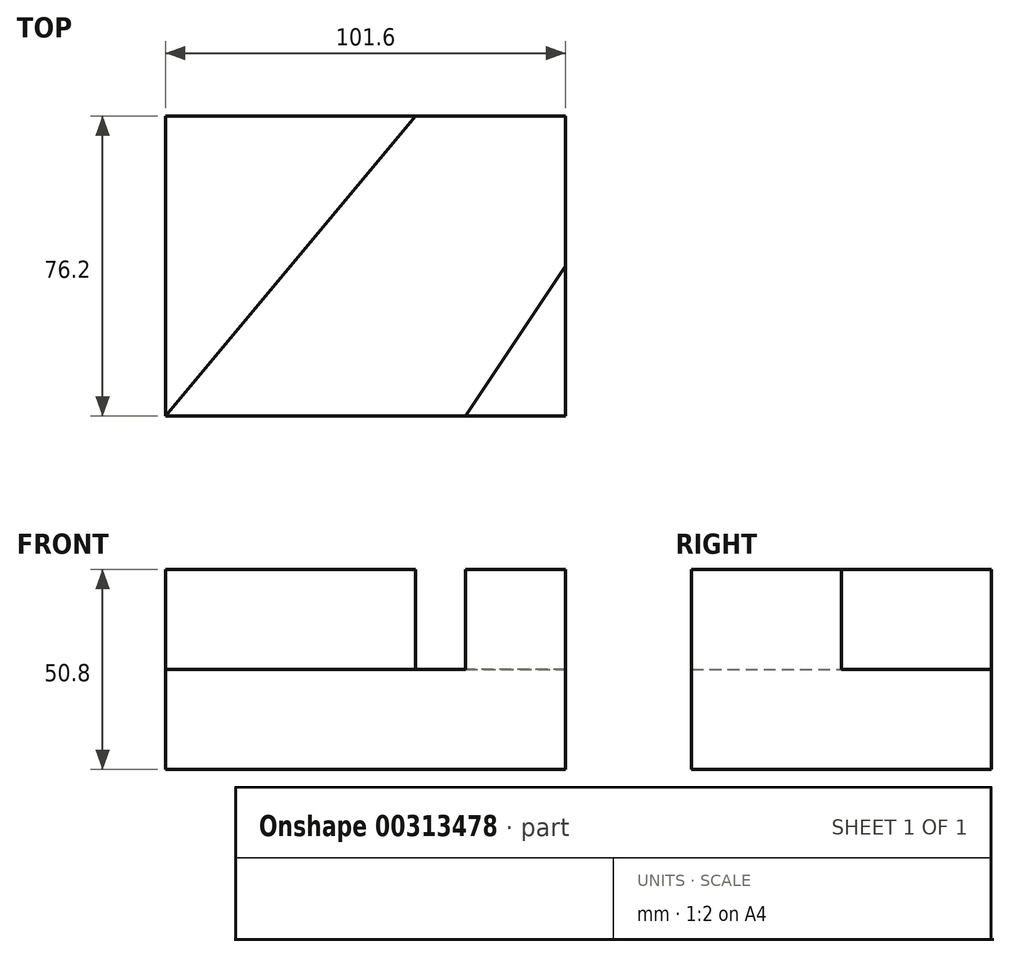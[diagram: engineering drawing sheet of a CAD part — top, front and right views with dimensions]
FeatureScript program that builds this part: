
annotation { "Feature Type Name" : "Feature", "Feature Type Description" : "" }
export const myFeature = defineFeature(function(context is Context, id is Id, definition is map)
    precondition{}
    {
        {
            var Q0;
            Q0=qCreatedBy(makeId("Top.planeOp"),FACE);
            var sketch = newSketch(context, id + "F0", { "sketchPlane" : qUnion([Q0])});
            skLineSegment(sketch, "E0", {"start": v(-53.76, -44.1) * mm, "end": v(47.84, -44.1) * mm});
            skLineSegment(sketch, "E1", {"start": v(47.84, -44.1) * mm, "end": v(47.84, 32.1) * mm});
            skLineSegment(sketch, "E2", {"start": v(47.84, 32.1) * mm, "end": v(-53.76, 32.1) * mm});
            skLineSegment(sketch, "E3", {"start": v(-53.76, 32.1) * mm, "end": v(-53.76, -44.1) * mm});
            skSolve(sketch);
        }
        {
            var Q0;
            Q0=makeQuery(id+"F0.imprint","IMPRINT",FACE,{"disambiguationData":[TD([[makeQuery(id+"F0.imprint","IMPRINT",EDGE,{"derivedFrom":sQuery(id+"F0.wireOp",EDGE,"E0")}),1.0]])]});
            extrude(context, id + "F1", {"entities" : qUnion([Q0]), "depth" : 25.4 * mm});
        }
        {
            var Q0;
            Q0=makeQuery(id+"F1.opExtrude","CAP_FACE",FACE,{"disambiguationData":[OSD([sQuery(id+"F0.wireOp",EDGE,"E0"),sQuery(id+"F0.wireOp",EDGE,"E1"),sQuery(id+"F0.wireOp",EDGE,"E2"),sQuery(id+"F0.wireOp",EDGE,"E3")])],"isStart":false});
            var sketch = newSketch(context, id + "F2", { "sketchPlane" : qUnion([Q0])});
            skLineSegment(sketch, "E4", {"start": v(22.44, -44.1) * mm, "end": v(47.84, -44.1) * mm});
            skLineSegment(sketch, "E5", {"start": v(47.84, -44.1) * mm, "end": v(47.84, -6) * mm});
            skLineSegment(sketch, "E6", {"start": v(22.44, -44.1) * mm, "end": v(47.84, -6) * mm});
            skSolve(sketch);
        }
        {
            var Q0;
            Q0=makeQuery(id+"F2.imprint","IMPRINT",FACE,{"disambiguationData":[TD([[makeQuery(id+"F2.imprint","IMPRINT",EDGE,{"derivedFrom":sQuery(id+"F2.wireOp",EDGE,"E4")}),1.0]])]});
            extrude(context, id + "F3", {"entities" : qUnion([Q0]), "operationType" : NewBodyOperationType.ADD, "depth" : 25.4 * mm});
        }
        {
            var Q0;
            Q0=makeQuery(id+"F1.opExtrude","CAP_FACE",FACE,{"disambiguationData":[OSD([sQuery(id+"F0.wireOp",EDGE,"E0"),sQuery(id+"F0.wireOp",EDGE,"E1"),sQuery(id+"F0.wireOp",EDGE,"E2"),sQuery(id+"F0.wireOp",EDGE,"E3")])],"isStart":false});
            var sketch = newSketch(context, id + "F4", { "sketchPlane" : qUnion([Q0])});
            skLineSegment(sketch, "E7", {"start": v(-53.76, -44.1) * mm, "end": v(-53.76, 32.1) * mm});
            skLineSegment(sketch, "E8", {"start": v(-53.76, 32.1) * mm, "end": v(9.74, 32.1) * mm});
            skLineSegment(sketch, "E9", {"start": v(-53.76, -44.1) * mm, "end": v(9.74, 32.1) * mm});
            skSolve(sketch);
        }
        {
            var Q0;
            Q0=makeQuery(id+"F4.imprint","IMPRINT",FACE,{"disambiguationData":[TD([[makeQuery(id+"F4.imprint","IMPRINT",EDGE,{"derivedFrom":sQuery(id+"F4.wireOp",EDGE,"E7")}),1.0]])]});
            extrude(context, id + "F5", {"entities" : qUnion([Q0]), "operationType" : NewBodyOperationType.ADD, "depth" : 25.4 * mm});
        }
    });
